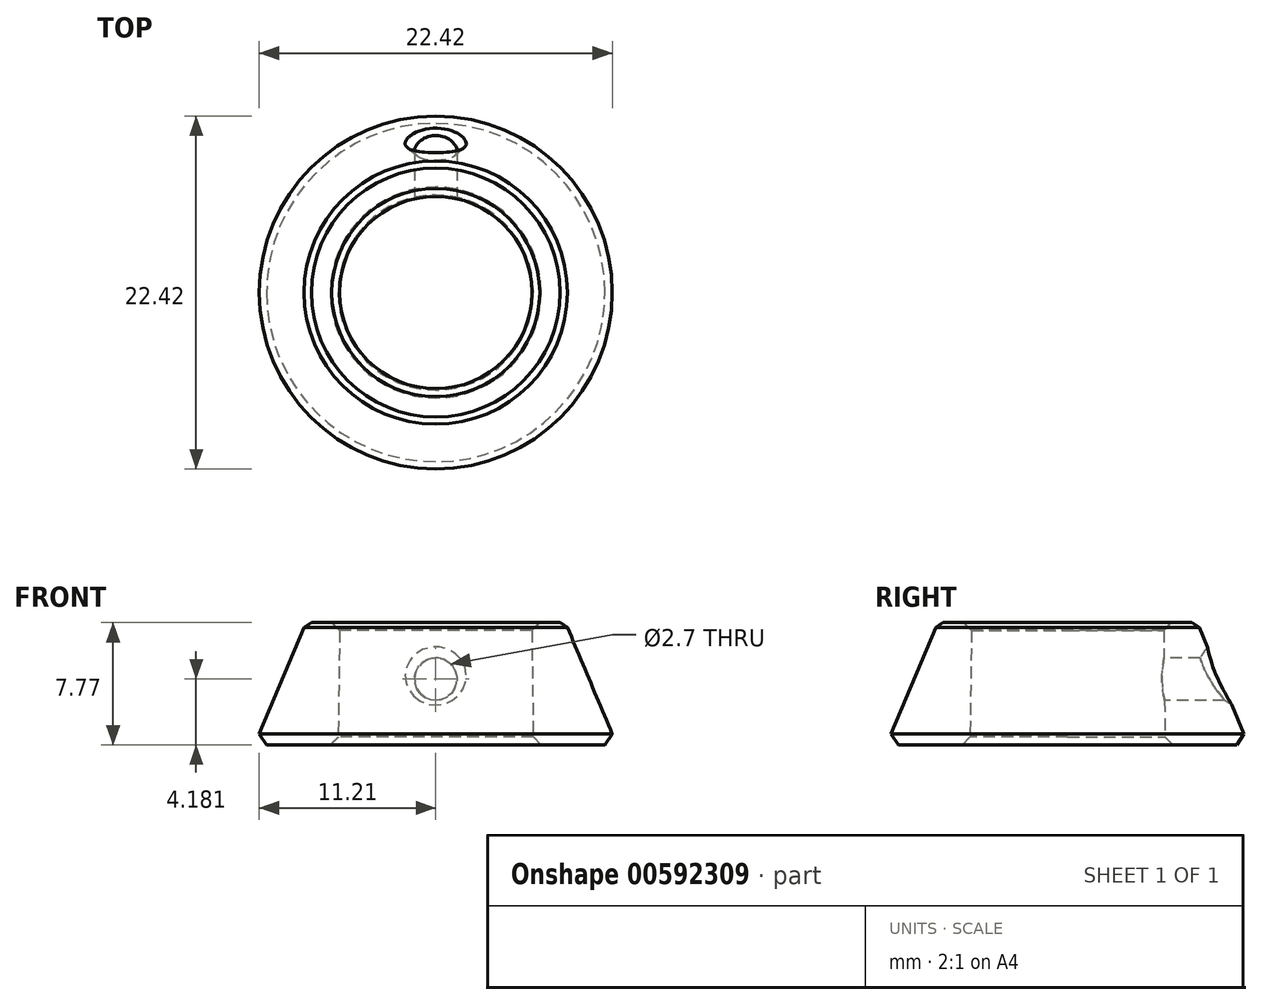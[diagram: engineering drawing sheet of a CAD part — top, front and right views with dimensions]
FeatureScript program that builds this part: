
annotation { "Feature Type Name" : "Feature", "Feature Type Description" : "" }
export const myFeature = defineFeature(function(context is Context, id is Id, definition is map)
    precondition{}
    {
        {
            var Q0;
            Q0=qCreatedBy(makeId("Front.planeOp"),FACE);
            var sketch = newSketch(context, id + "F0", { "sketchPlane" : qUnion([Q0])});
            skLineSegment(sketch, "E0", {"start": v(-6.1, 7.77) * mm, "end": v(-8.23, 7.77) * mm});
            skLineSegment(sketch, "E1", {"start": v(-8.23, 7.77) * mm, "end": v(-11.5, 0) * mm});
            skLineSegment(sketch, "E2", {"start": v(-11.5, 0) * mm, "end": v(-6.2, 0) * mm});
            skLineSegment(sketch, "E3", {"start": v(-6.2, 0) * mm, "end": v(-6.1, 7.77) * mm});
            skLineSegment(sketch, "E4", {"start": v(0, 8.98) * mm, "end": v(0, 0) * mm});
            skSolve(sketch);
        }
        {
            var Q0;
            Q0 = qSketchRegion(id + "F0", true);
            var Q1;
            Q1=sQuery(id+"F0.wireOp",EDGE,"E4");
            revolve(context, id + "F1", {"entities" : qUnion([Q0]), "axis" : qUnion([Q1]), "revolveType" : RevolveType.FULL});
        }
        {
            var Q0;
            Q0=makeQuery(id+"F1.opRevolve","SWEPT_EDGE",EDGE,{"disambiguationData":[OSD([sQuery(id+"F0.wireOp",EDGE,"E1"),sQuery(id+"F0.wireOp",EDGE,"E2")])]});
            var Q1;
            Q1=makeQuery(id+"F1.opRevolve","SWEPT_EDGE",EDGE,{"disambiguationData":[OSD([sQuery(id+"F0.wireOp",EDGE,"E0"),sQuery(id+"F0.wireOp",EDGE,"E1")])]});
            var Q2;
            Q2=makeQuery(id+"F1.opRevolve","SWEPT_EDGE",EDGE,{"disambiguationData":[OSD([sQuery(id+"F0.wireOp",EDGE,"E0"),sQuery(id+"F0.wireOp",EDGE,"E3")])]});
            var Q3;
            Q3=makeQuery(id+"F1.opRevolve","SWEPT_EDGE",EDGE,{"disambiguationData":[OSD([sQuery(id+"F0.wireOp",EDGE,"E2"),sQuery(id+"F0.wireOp",EDGE,"E3")])]});
            chamfer(context, id + "F2", {"entities" : qUnion([Q0, Q1, Q2, Q3]), "width" : 0.5 * mm, "tangentPropagation" : true});
        }
        {
            var Q0;
            Q0=qCreatedBy(makeId("Front.planeOp"),FACE);
            var sketch = newSketch(context, id + "F3", { "sketchPlane" : qUnion([Q0])});
            skCircle(sketch, "E5", {"center": v(0, 4.18) * mm, "radius": 1.35 * mm});
            skSolve(sketch);
        }
        {
            var Q0;
            Q0 = qSketchRegion(id + "F3", true);
            extrude(context, id + "F4", {"entities" : qUnion([Q0]), "operationType" : NewBodyOperationType.REMOVE, "oppositeDirection" : true, "depth" : 25 * mm, "offsetDistance" : 25 * mm});
        }
        {
            var Q0;
            Q0=makeQuery(id+"F4.boolean.opBoolean","INTERSECT",EDGE,{"derivedFrom":[makeQuery(id+"F1.opRevolve","SWEPT_FACE",FACE,{"disambiguationData":[OSD([sQuery(id+"F0.wireOp",EDGE,"E1")])]}),makeQuery(id+"F4.opExtrude","SWEPT_FACE",FACE,{"disambiguationData":[OSD([sQuery(id+"F3.wireOp",EDGE,"E5")])]})]});
            chamfer(context, id + "F5", {"entities" : qUnion([Q0]), "width" : 0.5 * mm, "tangentPropagation" : true});
        }
    });
